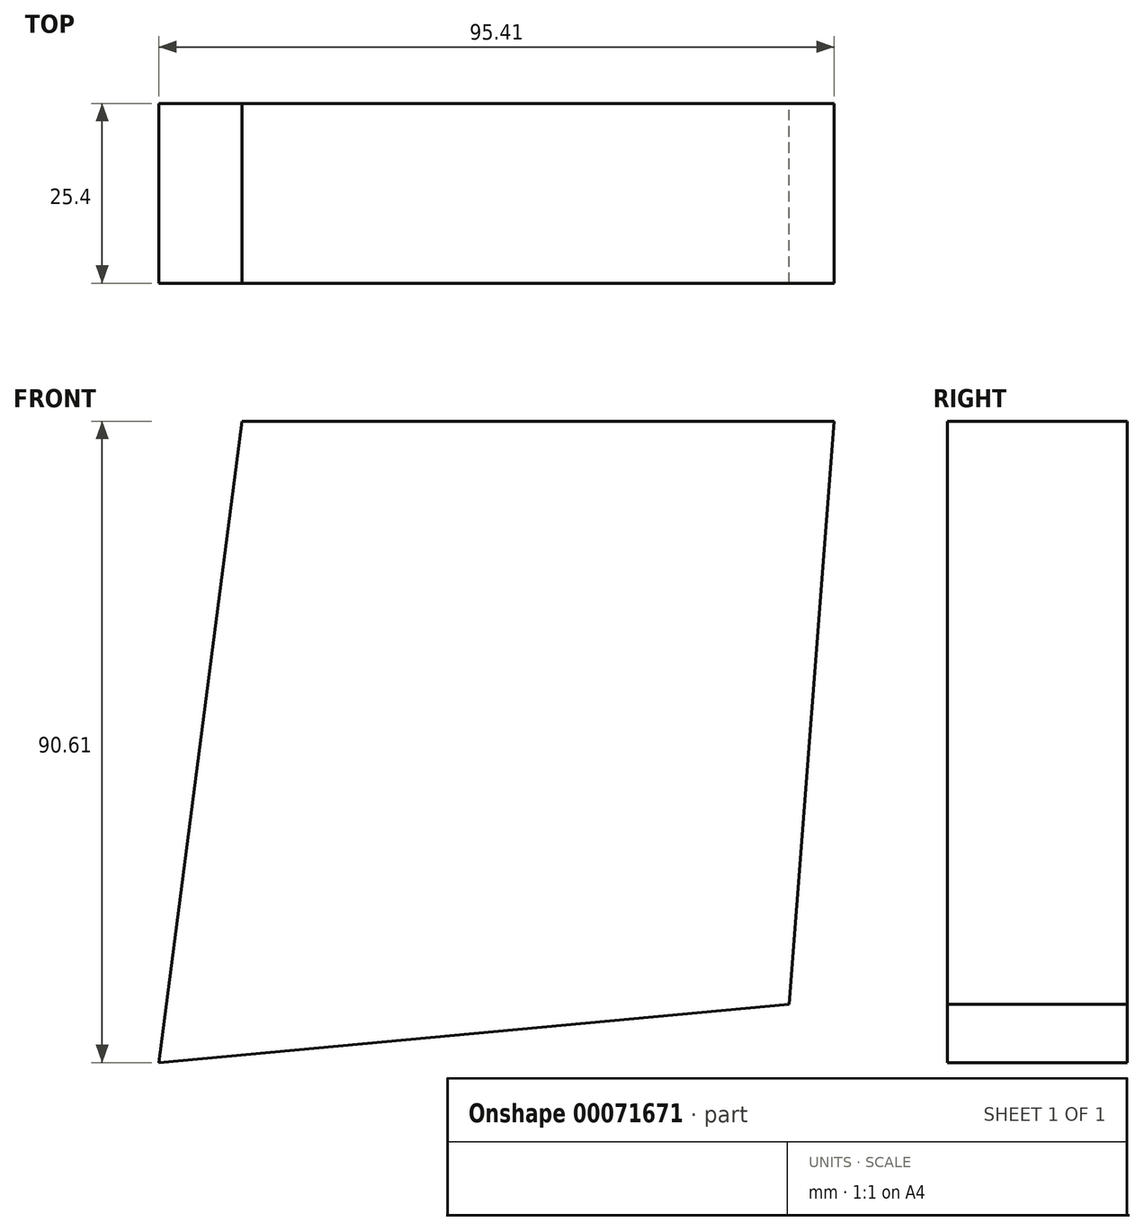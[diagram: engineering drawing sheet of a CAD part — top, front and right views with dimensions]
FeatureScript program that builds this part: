
annotation { "Feature Type Name" : "Feature", "Feature Type Description" : "" }
export const myFeature = defineFeature(function(context is Context, id is Id, definition is map)
    precondition{}
    {
        {
            var Q0;
            Q0=qCreatedBy(makeId("Front.planeOp"),FACE);
            var sketch = newSketch(context, id + "F0", { "sketchPlane" : qUnion([Q0])});
            skLineSegment(sketch, "E0", {"start": v(-55.9, 66.46) * mm, "end": v(27.77, 66.46) * mm});
            skLineSegment(sketch, "E1", {"start": v(27.77, 66.46) * mm, "end": v(21.36, -15.9) * mm});
            skLineSegment(sketch, "E2", {"start": v(21.36, -15.9) * mm, "end": v(-67.64, -24.15) * mm});
            skLineSegment(sketch, "E3", {"start": v(-67.64, -24.15) * mm, "end": v(-55.9, 66.46) * mm});
            skSolve(sketch);
        }
        {
            var Q0;
            Q0=makeQuery(id+"F0.imprint","IMPRINT",FACE,{"disambiguationData":[TD([[makeQuery(id+"F0.imprint","IMPRINT",EDGE,{"derivedFrom":sQuery(id+"F0.wireOp",EDGE,"E0")}),-1.0]])]});
            extrude(context, id + "F1", {"entities" : qUnion([Q0]), "depth" : 25.4 * mm});
        }
    });
